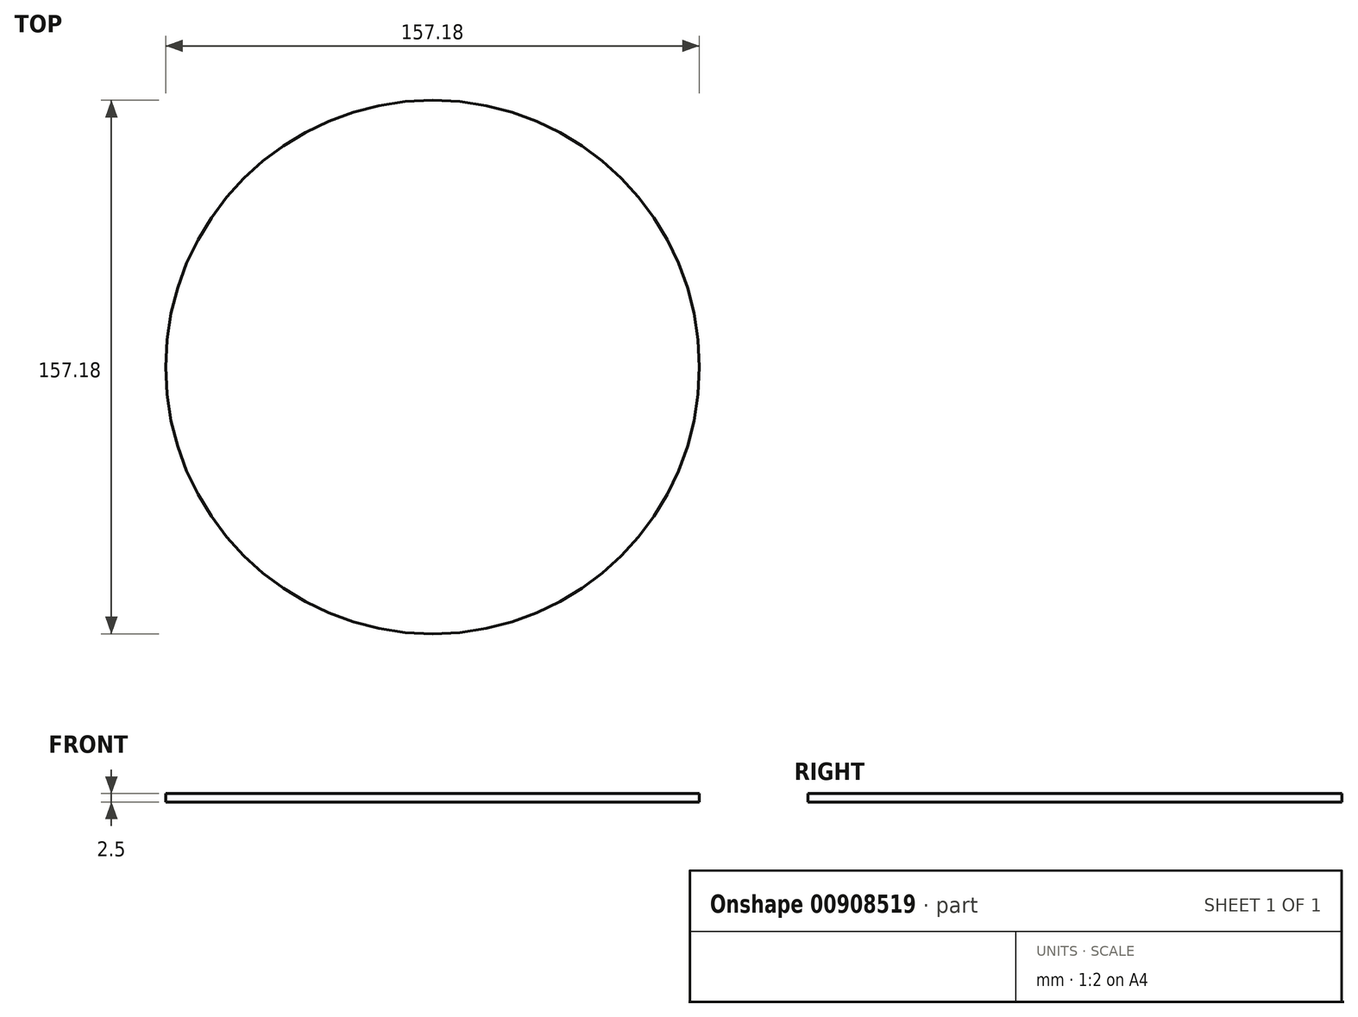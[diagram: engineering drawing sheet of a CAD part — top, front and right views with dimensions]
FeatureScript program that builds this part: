
annotation { "Feature Type Name" : "Feature", "Feature Type Description" : "" }
export const myFeature = defineFeature(function(context is Context, id is Id, definition is map)
    precondition{}
    {
        {
            var Q0;
            Q0=qCreatedBy(makeId("Top.planeOp"),FACE);
            var sketch = newSketch(context, id + "F0", { "sketchPlane" : qUnion([Q0])});
            skArc(sketch, "E0", {"start": v(0, 67.54) * mm, "mid": v(-30.14, 72.77) * mm, "end": v(-47.76, 47.76) * mm});
            skArc(sketch, "E1.1.0", {"start": v(-47.76, 47.76) * mm, "mid": v(-72.77, 30.14) * mm, "end": v(-67.54, 0) * mm});
            skArc(sketch, "E1.2.0", {"start": v(-67.54, 0) * mm, "mid": v(-72.77, -30.14) * mm, "end": v(-47.76, -47.76) * mm});
            skPoint(sketch, "E1.center", {"position": v(0, 0) * mm});
            skArc(sketch, "E2.3.3.0", {"start": v(-47.76, -47.76) * mm, "mid": v(-30.14, -72.77) * mm, "end": v(0, -67.54) * mm});
            skArc(sketch, "E2.3.4.0", {"start": v(0, -67.54) * mm, "mid": v(30.14, -72.77) * mm, "end": v(47.76, -47.76) * mm});
            skArc(sketch, "E2.3.5.0", {"start": v(47.76, -47.76) * mm, "mid": v(72.77, -30.14) * mm, "end": v(67.54, 0) * mm});
            skArc(sketch, "E2.3.6.0", {"start": v(67.54, 0) * mm, "mid": v(72.77, 30.14) * mm, "end": v(47.76, 47.76) * mm});
            skArc(sketch, "E2.3.7.0", {"start": v(47.76, 47.76) * mm, "mid": v(30.14, 72.77) * mm, "end": v(0, 67.54) * mm});
            skSolve(sketch);
        }
        {
            var Q0;
            Q0=qCreatedBy(makeId("Top.planeOp"),FACE);
            var Q1;
            Q1=makeQuery(id+"F0.imprint","IMPRINT",FACE,{"disambiguationData":[TD([[makeQuery(id+"F0.imprint","IMPRINT",EDGE,{"derivedFrom":sQuery(id+"F0.wireOp",EDGE,"20dG0tCf-75TG-ht6W-R5EH-glOTCc1QS95o")}),-1.0]])]});
            cPlane(context, id + "F1", {"entities" : qUnion([Q0, Q1]), "cplaneType" : CPlaneType.OFFSET, "offset" : 128 * mm, "width" : 150 * mm, "height" : 150 * mm});
        }
        {
            var Q0;
            Q0=qCreatedBy(id+"F1.planeOp",FACE);
            var sketch = newSketch(context, id + "F2", { "sketchPlane" : qUnion([Q0])});
            skPoint(sketch, "E3", {"position": v(0, 0) * mm});
            skSolve(sketch);
        }
        {
            var Q0;
            Q0=makeQuery(id+"F0.imprint","IMPRINT",FACE,{"disambiguationData":[TD([[makeQuery(id+"F0.imprint","IMPRINT",EDGE,{"derivedFrom":sQuery(id+"F0.wireOp",EDGE,"E0")}),1.0]])]});
            var Q1;
            Q1=sQuery(id+"F2.wireOp",VERTEX,"E3");
            var Q2;
            Q2=makeQuery(id+"F0.imprint","IMPRINT",FACE,{"disambiguationData":[TD([[makeQuery(id+"F0.imprint","IMPRINT",EDGE,{"derivedFrom":sQuery(id+"F0.wireOp",EDGE,"E0")}),1.0]])]});
            var Q3;
            Q3=sQuery(id+"F2.wireOp",VERTEX,"E3");
            loft(context, id + "F3", {"bodyType" : ToolBodyType.SURFACE, "sheetProfilesArray" : [{ "sheetProfileEntities" : qUnion([Q0]) }, { "sheetProfileEntities" : qUnion([Q1]) }], "wireProfilesArray" : [{ "wireProfileEntities" : qUnion([Q2]) }, { "wireProfileEntities" : qUnion([Q3]) }]});
        }
        {
            var Q0;
            Q0=qCreatedBy(makeId("Top.planeOp"),FACE);
            cPlane(context, id + "F4", {"entities" : qUnion([Q0]), "cplaneType" : CPlaneType.OFFSET, "offset" : 47 * mm, "oppositeDirection" : true, "width" : 150 * mm, "height" : 150 * mm});
        }
        {
            var Q0;
            Q0=makeQuery(id+"F3.opLoft","SWEPT_BODY",BODY,{"disambiguationData":[OSD([sQuery(id+"F0.wireOp",EDGE,"E2.3.4.0"),sQuery(id+"F2.wireOp",VERTEX,"E3")])]});
            var Q1;
            Q1=qCreatedBy(id+"F4.planeOp",FACE);
            mirror(context, id + "F5", {"entities" : qUnion([Q0]), "mirrorPlane" : qUnion([Q1])});
        }
        {
            var Q0;
            Q0=qCreatedBy(id+"F4.planeOp",FACE);
            var sketch = newSketch(context, id + "F6", { "sketchPlane" : qUnion([Q0])});
            skCircle(sketch, "E4", {"center": v(0, 0) * mm, "radius": 78.6 * mm});
            skSolve(sketch);
        }
        {
            var Q0;
            Q0=makeQuery(id+"F6.imprint","IMPRINT",FACE,{"disambiguationData":[TD([[makeQuery(id+"F6.imprint","IMPRINT",EDGE,{"derivedFrom":sQuery(id+"F6.wireOp",EDGE,"E4")}),1.0]])]});
            extrude(context, id + "F7", {"entities" : qUnion([Q0]), "depth" : 2.5 * mm, "offsetDistance" : 25 * mm});
        }
    });
